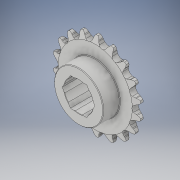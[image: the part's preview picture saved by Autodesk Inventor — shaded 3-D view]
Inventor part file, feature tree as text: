
AUTODESK INVENTOR PART (.ipt)
format: ipt  version: 2018 (Build 220112000, 112)  size: 542,208 bytes
history: native  units: in
note: dims shown in document units (in); Inventor stores cm internally (conversion verified against a paired STEP export)
features: chamfer x1
ambient origin geometry x8: Origin, YZ Plane, XZ Plane, XY Plane, X Axis, Y Axis, Z Axis, Center Point
bodies: Solid1 (feature_tree)
feature tree (1):
  chamfer  "Chamfer2"  [1 undecoded]
note: 1 required parameter value undecoded (feature->parameter linkage not recoverable at this tier; creation-order binding heuristic only, values carry confidence <= 0.55)
